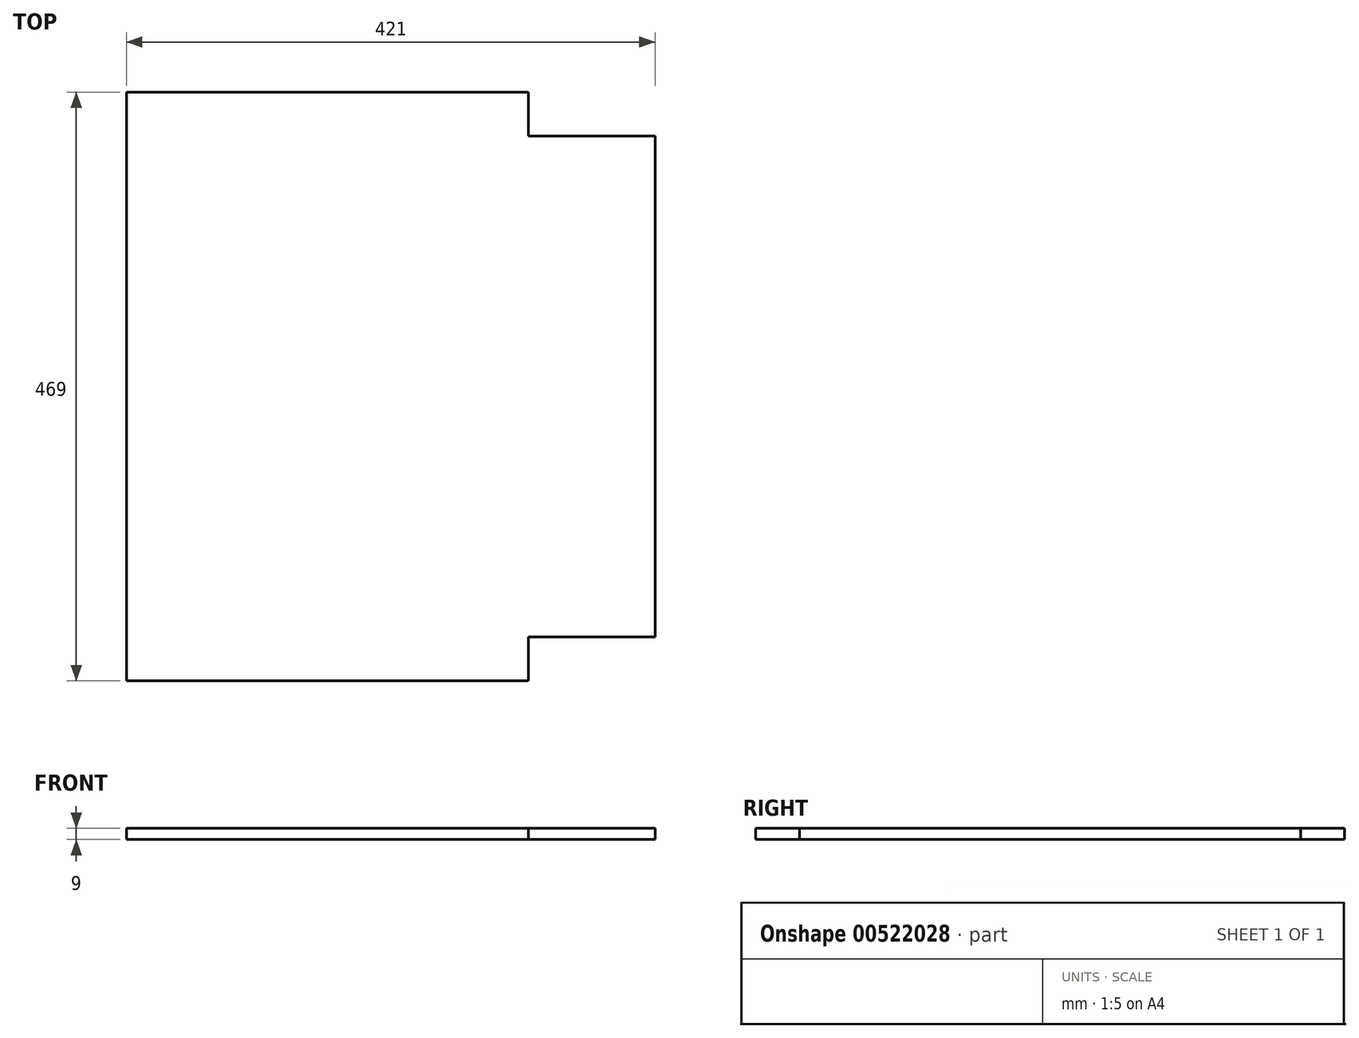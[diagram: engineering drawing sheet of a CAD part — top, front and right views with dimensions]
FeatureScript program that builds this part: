
annotation { "Feature Type Name" : "Feature", "Feature Type Description" : "" }
export const myFeature = defineFeature(function(context is Context, id is Id, definition is map)
    precondition{}
    {
        {
            var Q0;
            Q0=qCreatedBy(makeId("Top.planeOp"),FACE);
            var sketch = newSketch(context, id + "F0", { "sketchPlane" : qUnion([Q0])});
            skLineSegment(sketch, "E0.bottom", {"start": v(0, 0) * mm, "end": v(320, 0) * mm});
            skLineSegment(sketch, "E0.top", {"start": v(0, 469) * mm, "end": v(320, 469) * mm});
            skLineSegment(sketch, "E0.left", {"start": v(0, 0) * mm, "end": v(0, 469) * mm});
            skLineSegment(sketch, "E0.right", {"start": v(421, 35) * mm, "end": v(421, 434) * mm});
            skLineSegment(sketch, "E1", {"start": v(320, 0) * mm, "end": v(320, 35) * mm});
            skLineSegment(sketch, "E2", {"start": v(320, 35) * mm, "end": v(421, 35) * mm});
            skLineSegment(sketch, "E3", {"start": v(421, 434) * mm, "end": v(320, 434) * mm});
            skLineSegment(sketch, "E4", {"start": v(320, 434) * mm, "end": v(320, 469) * mm});
            skSolve(sketch);
        }
        {
            var Q0;
            Q0=makeQuery(id+"F0.imprint","IMPRINT",FACE,{"disambiguationData":[TD([[makeQuery(id+"F0.imprint","IMPRINT",EDGE,{"derivedFrom":sQuery(id+"F0.wireOp",EDGE,"E0.bottom")}),1.0]])]});
            extrude(context, id + "F1", {"entities" : qUnion([Q0]), "depth" : 9 * mm, "offsetDistance" : 25 * mm});
        }
    });
